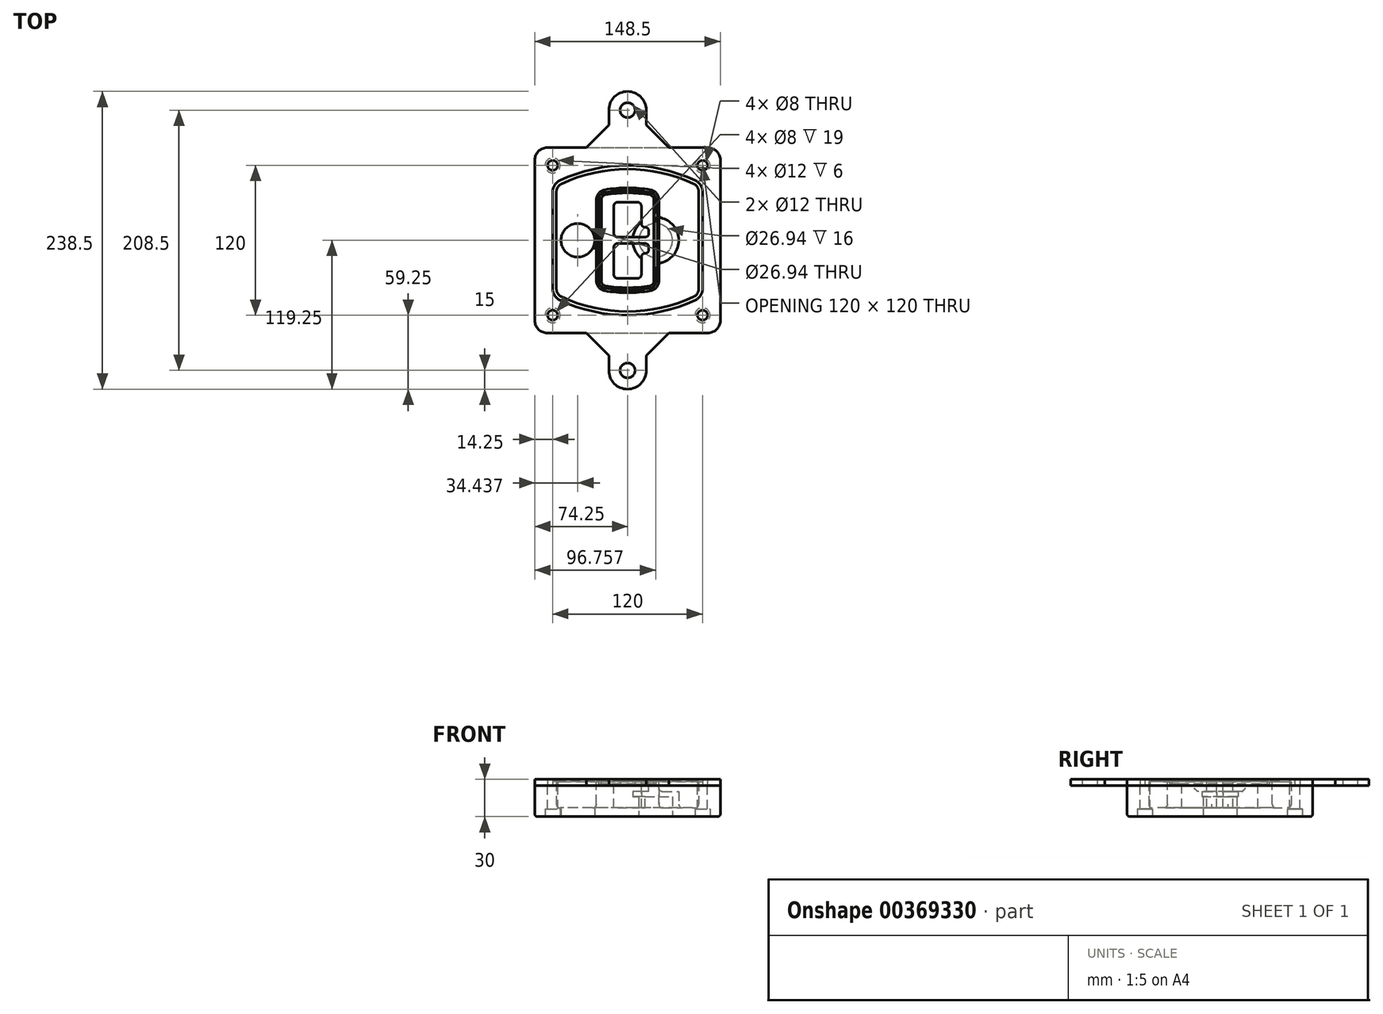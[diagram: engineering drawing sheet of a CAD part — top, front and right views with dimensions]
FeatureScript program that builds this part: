
annotation { "Feature Type Name" : "Feature", "Feature Type Description" : "" }
export const myFeature = defineFeature(function(context is Context, id is Id, definition is map)
    precondition{}
    {
        {
            var Q0;
            Q0=qCreatedBy(makeId("Top.planeOp"),FACE);
            var sketch = newSketch(context, id + "F0", { "sketchPlane" : qUnion([Q0])});
            skPoint(sketch, "E0.rect.middle", {"position": v(0, 0) * mm});
            skLineSegment(sketch, "E1.bottom", {"start": v(-64.25, -74.25) * mm, "end": v(64.25, -74.25) * mm});
            skLineSegment(sketch, "E1.top", {"start": v(-64.25, 74.25) * mm, "end": v(64.25, 74.25) * mm});
            skLineSegment(sketch, "E1.left", {"start": v(-74.25, -64.25) * mm, "end": v(-74.25, 64.25) * mm});
            skLineSegment(sketch, "E1.right", {"start": v(74.25, -64.25) * mm, "end": v(74.25, 64.25) * mm});
            skLineSegment(sketch, "E2", {"start": v(-74.25, 74.25) * mm, "end": v(74.25, -74.25) * mm, "construction": true});
            skLineSegment(sketch, "E3", {"start": v(74.25, 74.25) * mm, "end": v(-74.25, -74.25) * mm, "construction": true});
            skCircle(sketch, "E4", {"center": v(-60, 60) * mm, "radius": 4 * mm});
            skCircle(sketch, "E5", {"center": v(60, 60) * mm, "radius": 4 * mm});
            skCircle(sketch, "E6", {"center": v(60, -60) * mm, "radius": 4 * mm});
            skCircle(sketch, "E7", {"center": v(-60, -60) * mm, "radius": 4 * mm});
            skLineSegment(sketch, "E8", {"start": v(-60, 60) * mm, "end": v(60, 60) * mm, "construction": true});
            skLineSegment(sketch, "E9", {"start": v(60, 60) * mm, "end": v(60, -60) * mm, "construction": true});
            skLineSegment(sketch, "E10", {"start": v(60, -60) * mm, "end": v(-60, -60) * mm, "construction": true});
            skLineSegment(sketch, "E11", {"start": v(-60, -60) * mm, "end": v(-60, 60) * mm, "construction": true});
            skLineSegment(sketch, "E12", {"start": v(-60, 38.83) * mm, "end": v(-60, -38.83) * mm});
            skLineSegment(sketch, "E13", {"start": v(60, 38.83) * mm, "end": v(60, -38.83) * mm});
            skArc(sketch, "E14", {"start": v(54.26, 47.88) * mm, "mid": v(0, 60) * mm, "end": v(-54.26, 47.88) * mm});
            skArc(sketch, "E15", {"start": v(-54.26, -47.88) * mm, "mid": v(0, -60) * mm, "end": v(54.26, -47.88) * mm});
            skLineSegment(sketch, "E16", {"start": v(-60, 0) * mm, "end": v(60, 0) * mm, "construction": true});
            skPoint(sketch, "E17.visualSharp", {"position": v(-60, -45) * mm});
            skArc(sketch, "E17.filletArc", {"start": v(-60, -38.83) * mm, "mid": v(-58.44, -44.2) * mm, "end": v(-54.26, -47.88) * mm});
            skPoint(sketch, "E18.visualSharp", {"position": v(-60, 45) * mm});
            skArc(sketch, "E18.filletArc", {"start": v(-54.26, 47.88) * mm, "mid": v(-58.44, 44.2) * mm, "end": v(-60, 38.83) * mm});
            skPoint(sketch, "E19.visualSharp", {"position": v(60, 45) * mm});
            skArc(sketch, "E19.filletArc", {"start": v(60, 38.83) * mm, "mid": v(58.44, 44.2) * mm, "end": v(54.26, 47.88) * mm});
            skPoint(sketch, "E20.visualSharp", {"position": v(60, -45) * mm});
            skArc(sketch, "E20.filletArc", {"start": v(54.26, -47.88) * mm, "mid": v(58.44, -44.2) * mm, "end": v(60, -38.83) * mm});
            skPoint(sketch, "E21.visualSharp", {"position": v(-74.25, 74.25) * mm});
            skArc(sketch, "E21.filletArc", {"start": v(-64.25, 74.25) * mm, "mid": v(-71.32, 71.32) * mm, "end": v(-74.25, 64.25) * mm});
            skPoint(sketch, "E22.visualSharp", {"position": v(74.25, 74.25) * mm});
            skArc(sketch, "E22.filletArc", {"start": v(74.25, 64.25) * mm, "mid": v(71.32, 71.32) * mm, "end": v(64.25, 74.25) * mm});
            skPoint(sketch, "E23.visualSharp", {"position": v(74.25, -74.25) * mm});
            skArc(sketch, "E23.filletArc", {"start": v(64.25, -74.25) * mm, "mid": v(71.32, -71.32) * mm, "end": v(74.25, -64.25) * mm});
            skPoint(sketch, "E24.visualSharp", {"position": v(-74.25, -74.25) * mm});
            skArc(sketch, "E24.filletArc", {"start": v(-74.25, -64.25) * mm, "mid": v(-71.32, -71.32) * mm, "end": v(-64.25, -74.25) * mm});
            skArc(sketch, "E25.0", {"start": v(57, 38.83) * mm, "mid": v(55.9, 42.58) * mm, "end": v(52.98, 45.17) * mm});
            skLineSegment(sketch, "E25.1", {"start": v(57, 38.83) * mm, "end": v(57, -38.83) * mm});
            skArc(sketch, "E25.2", {"start": v(52.98, -45.17) * mm, "mid": v(55.9, -42.58) * mm, "end": v(57, -38.83) * mm});
            skArc(sketch, "E25.3", {"start": v(-52.98, -45.17) * mm, "mid": v(0, -57) * mm, "end": v(52.98, -45.17) * mm});
            skArc(sketch, "E25.4", {"start": v(-57, -38.83) * mm, "mid": v(-55.9, -42.58) * mm, "end": v(-52.98, -45.17) * mm});
            skArc(sketch, "E25.5", {"start": v(52.98, 45.17) * mm, "mid": v(0, 57) * mm, "end": v(-52.98, 45.17) * mm});
            skLineSegment(sketch, "E25.6", {"start": v(-57, 38.83) * mm, "end": v(-57, -38.83) * mm});
            skArc(sketch, "E25.7", {"start": v(-52.98, 45.17) * mm, "mid": v(-55.9, 42.58) * mm, "end": v(-57, 38.83) * mm});
            skArc(sketch, "E26.0", {"start": v(-55.96, 51.5) * mm, "mid": v(-61.82, 46.33) * mm, "end": v(-64, 38.83) * mm});
            skArc(sketch, "E26.1", {"start": v(55.96, 51.5) * mm, "mid": v(0, 64) * mm, "end": v(-55.96, 51.5) * mm});
            skArc(sketch, "E26.2", {"start": v(64, 38.83) * mm, "mid": v(61.82, 46.33) * mm, "end": v(55.96, 51.5) * mm});
            skLineSegment(sketch, "E26.3", {"start": v(64, 38.83) * mm, "end": v(64, -38.83) * mm});
            skArc(sketch, "E26.4", {"start": v(55.96, -51.5) * mm, "mid": v(61.82, -46.33) * mm, "end": v(64, -38.83) * mm});
            skLineSegment(sketch, "E26.5", {"start": v(-64, 38.83) * mm, "end": v(-64, -38.83) * mm});
            skArc(sketch, "E26.6", {"start": v(-55.96, -51.5) * mm, "mid": v(0, -64) * mm, "end": v(55.96, -51.5) * mm});
            skArc(sketch, "E26.7", {"start": v(-64, -38.83) * mm, "mid": v(-61.82, -46.33) * mm, "end": v(-55.96, -51.5) * mm});
            skSolve(sketch);
        }
        {
            var Q0;
            Q0=makeQuery(id+"F0.imprint","IMPRINT",FACE,{"disambiguationData":[TD([[makeQuery(id+"F0.imprint","IMPRINT",EDGE,{"derivedFrom":sQuery(id+"F0.wireOp",EDGE,"E1.bottom")}),1.0]])]});
            var Q1;
            Q1=makeQuery(id+"F0.imprint","IMPRINT",FACE,{"disambiguationData":[TD([[makeQuery(id+"F0.imprint","IMPRINT",EDGE,{"derivedFrom":sQuery(id+"F0.wireOp",EDGE,"E12")}),1.0]])]});
            var Q2;
            Q2=makeQuery(id+"F0.imprint","IMPRINT",FACE,{"disambiguationData":[TD([[makeQuery(id+"F0.imprint","IMPRINT",EDGE,{"derivedFrom":sQuery(id+"F0.wireOp",EDGE,"E25.0")}),1.0]])]});
            var Q3;
            Q3=makeQuery(id+"F0.imprint","IMPRINT",FACE,{"disambiguationData":[TD([[makeQuery(id+"F0.imprint","IMPRINT",EDGE,{"derivedFrom":sQuery(id+"F0.wireOp",EDGE,"E12")}),-1.0]])]});
            extrude(context, id + "F1", {"entities" : qUnion([Q0, Q1, Q2, Q3]), "oppositeDirection" : true, "depth" : 25 * mm});
        }
        {
            var Q0;
            Q0=makeQuery(id+"F0.imprint","IMPRINT",FACE,{"disambiguationData":[TD([[makeQuery(id+"F0.imprint","IMPRINT",EDGE,{"derivedFrom":sQuery(id+"F0.wireOp",EDGE,"E12")}),1.0]])]});
            extrude(context, id + "F2", {"entities" : qUnion([Q0]), "operationType" : NewBodyOperationType.ADD, "depth" : 3 * mm});
        }
        {
            var Q0;
            Q0=makeQuery(id+"F0.imprint","IMPRINT",FACE,{"disambiguationData":[TD([[makeQuery(id+"F0.imprint","IMPRINT",EDGE,{"derivedFrom":sQuery(id+"F0.wireOp",EDGE,"E25.0")}),1.0]])]});
            extrude(context, id + "F3", {"entities" : qUnion([Q0]), "operationType" : NewBodyOperationType.REMOVE, "oppositeDirection" : true, "depth" : 18 * mm});
        }
        {
            var Q0;
            Q0=makeQuery(id+"F2.opExtrude","CAP_FACE",FACE,{"disambiguationData":[OSD([sQuery(id+"F0.wireOp",EDGE,"E12"),sQuery(id+"F0.wireOp",EDGE,"E13"),sQuery(id+"F0.wireOp",EDGE,"E14"),sQuery(id+"F0.wireOp",EDGE,"E15"),sQuery(id+"F0.wireOp",EDGE,"E17.filletArc"),sQuery(id+"F0.wireOp",EDGE,"E18.filletArc"),sQuery(id+"F0.wireOp",EDGE,"E19.filletArc"),sQuery(id+"F0.wireOp",EDGE,"E20.filletArc"),sQuery(id+"F0.wireOp",EDGE,"E25.0"),sQuery(id+"F0.wireOp",EDGE,"E25.1"),sQuery(id+"F0.wireOp",EDGE,"E25.2"),sQuery(id+"F0.wireOp",EDGE,"E25.3"),sQuery(id+"F0.wireOp",EDGE,"E25.4"),sQuery(id+"F0.wireOp",EDGE,"E25.5"),sQuery(id+"F0.wireOp",EDGE,"E25.6"),sQuery(id+"F0.wireOp",EDGE,"E25.7")])],"isStart":false});
            var sketch = newSketch(context, id + "F4", { "sketchPlane" : qUnion([Q0])});
            skArc(sketch, "E27.0", {"start": v(-18.34, -40.45) * mm, "mid": v(0, -42) * mm, "end": v(18.34, -40.45) * mm});
            skArc(sketch, "E28.0", {"start": v(18.34, 40.45) * mm, "mid": v(0, 42) * mm, "end": v(-18.34, 40.45) * mm});
            skLineSegment(sketch, "E29", {"start": v(-25, 32.57) * mm, "end": v(-25, -32.57) * mm});
            skLineSegment(sketch, "E30", {"start": v(25, 32.57) * mm, "end": v(25, -32.57) * mm});
            skLineSegment(sketch, "E31", {"start": v(-25, 39.1) * mm, "end": v(25, 39.1) * mm, "construction": true});
            skLineSegment(sketch, "E32", {"start": v(-25, -39.1) * mm, "end": v(25, -39.1) * mm, "construction": true});
            skPoint(sketch, "E33.visualSharp", {"position": v(-25, 39.1) * mm});
            skArc(sketch, "E33.filletArc", {"start": v(-18.34, 40.45) * mm, "mid": v(-23.11, 37.73) * mm, "end": v(-25, 32.57) * mm});
            skPoint(sketch, "E34.visualSharp", {"position": v(25, 39.1) * mm});
            skArc(sketch, "E34.filletArc", {"start": v(25, 32.57) * mm, "mid": v(23.11, 37.73) * mm, "end": v(18.34, 40.45) * mm});
            skPoint(sketch, "E35.visualSharp", {"position": v(25, -39.1) * mm});
            skArc(sketch, "E35.filletArc", {"start": v(18.34, -40.45) * mm, "mid": v(23.11, -37.73) * mm, "end": v(25, -32.57) * mm});
            skPoint(sketch, "E36.visualSharp", {"position": v(-25, -39.1) * mm});
            skArc(sketch, "E36.filletArc", {"start": v(-25, -32.57) * mm, "mid": v(-23.11, -37.73) * mm, "end": v(-18.34, -40.45) * mm});
            skArc(sketch, "E37.0", {"start": v(52.98, 45.17) * mm, "mid": v(0, 57) * mm, "end": v(-52.98, 45.17) * mm});
            skArc(sketch, "E37.1", {"start": v(-52.98, 45.17) * mm, "mid": v(-55.9, 42.58) * mm, "end": v(-57, 38.83) * mm});
            skLineSegment(sketch, "E37.2", {"start": v(-57, 38.83) * mm, "end": v(-57, -38.83) * mm});
            skArc(sketch, "E37.3", {"start": v(-57, -38.83) * mm, "mid": v(-55.9, -42.58) * mm, "end": v(-52.98, -45.17) * mm});
            skArc(sketch, "E37.4", {"start": v(-52.98, -45.17) * mm, "mid": v(0, -57) * mm, "end": v(52.98, -45.17) * mm});
            skArc(sketch, "E37.5", {"start": v(52.98, -45.17) * mm, "mid": v(55.9, -42.58) * mm, "end": v(57, -38.83) * mm});
            skLineSegment(sketch, "E37.6", {"start": v(57, 38.83) * mm, "end": v(57, -38.83) * mm});
            skArc(sketch, "E37.7", {"start": v(57, 38.83) * mm, "mid": v(55.9, 42.58) * mm, "end": v(52.98, 45.17) * mm});
            skLineSegment(sketch, "E38.0", {"start": v(23, 32.57) * mm, "end": v(23, -32.57) * mm});
            skArc(sketch, "E38.1", {"start": v(18, -38.48) * mm, "mid": v(21.58, -36.44) * mm, "end": v(23, -32.57) * mm});
            skArc(sketch, "E38.2", {"start": v(-18, -38.48) * mm, "mid": v(0, -40) * mm, "end": v(18, -38.48) * mm});
            skArc(sketch, "E38.3", {"start": v(-23, -32.57) * mm, "mid": v(-21.58, -36.44) * mm, "end": v(-18, -38.48) * mm});
            skLineSegment(sketch, "E38.4", {"start": v(-23, 32.57) * mm, "end": v(-23, -32.57) * mm});
            skArc(sketch, "E38.5", {"start": v(23, 32.57) * mm, "mid": v(21.58, 36.44) * mm, "end": v(18, 38.48) * mm});
            skArc(sketch, "E38.6", {"start": v(-18, 38.48) * mm, "mid": v(-21.58, 36.44) * mm, "end": v(-23, 32.57) * mm});
            skArc(sketch, "E38.7", {"start": v(18, 38.48) * mm, "mid": v(0, 40) * mm, "end": v(-18, 38.48) * mm});
            skArc(sketch, "E39.0", {"start": v(21, 32.57) * mm, "mid": v(20.06, 35.15) * mm, "end": v(17.67, 36.5) * mm});
            skLineSegment(sketch, "E39.1", {"start": v(21, 32.57) * mm, "end": v(21, -32.57) * mm});
            skArc(sketch, "E39.2", {"start": v(17.67, -36.5) * mm, "mid": v(20.06, -35.15) * mm, "end": v(21, -32.57) * mm});
            skArc(sketch, "E39.3", {"start": v(-17.67, -36.5) * mm, "mid": v(0, -38) * mm, "end": v(17.67, -36.5) * mm});
            skArc(sketch, "E39.4", {"start": v(-21, -32.57) * mm, "mid": v(-20.06, -35.15) * mm, "end": v(-17.67, -36.5) * mm});
            skArc(sketch, "E39.5", {"start": v(17.67, 36.5) * mm, "mid": v(0, 38) * mm, "end": v(-17.67, 36.5) * mm});
            skLineSegment(sketch, "E39.6", {"start": v(-21, 32.57) * mm, "end": v(-21, -32.57) * mm});
            skArc(sketch, "E39.7", {"start": v(-17.67, 36.5) * mm, "mid": v(-20.06, 35.15) * mm, "end": v(-21, 32.57) * mm});
            skLineSegment(sketch, "E40", {"start": v(-25, 0) * mm, "end": v(25, 0) * mm, "construction": true});
            skLineSegment(sketch, "E41", {"start": v(-11, 5.5) * mm, "end": v(-11, 27.5) * mm});
            skLineSegment(sketch, "E42", {"start": v(-8, 30.5) * mm, "end": v(8, 30.5) * mm});
            skLineSegment(sketch, "E43", {"start": v(11, 27.5) * mm, "end": v(11, 13.5) * mm});
            skLineSegment(sketch, "E44", {"start": v(14, 10.5) * mm, "end": v(14, 10.5) * mm});
            skLineSegment(sketch, "E45", {"start": v(17, 7.5) * mm, "end": v(17, 5.5) * mm});
            skLineSegment(sketch, "E46", {"start": v(14, 2.5) * mm, "end": v(-8, 2.5) * mm});
            skPoint(sketch, "E47.visualSharp", {"position": v(-11, 30.5) * mm});
            skArc(sketch, "E47.filletArc", {"start": v(-8, 30.5) * mm, "mid": v(-10.12, 29.62) * mm, "end": v(-11, 27.5) * mm});
            skPoint(sketch, "E48.visualSharp", {"position": v(11, 30.5) * mm});
            skArc(sketch, "E48.filletArc", {"start": v(11, 27.5) * mm, "mid": v(10.12, 29.62) * mm, "end": v(8, 30.5) * mm});
            skPoint(sketch, "E49.visualSharp", {"position": v(11, 10.5) * mm});
            skArc(sketch, "E49.filletArc", {"start": v(11, 13.5) * mm, "mid": v(11.88, 11.38) * mm, "end": v(14, 10.5) * mm});
            skPoint(sketch, "E50.visualSharp", {"position": v(17, 10.5) * mm});
            skArc(sketch, "E50.filletArc", {"start": v(17, 7.5) * mm, "mid": v(16.12, 9.62) * mm, "end": v(14, 10.5) * mm});
            skPoint(sketch, "E51.visualSharp", {"position": v(17, 2.5) * mm});
            skArc(sketch, "E51.filletArc", {"start": v(14, 2.5) * mm, "mid": v(16.12, 3.38) * mm, "end": v(17, 5.5) * mm});
            skPoint(sketch, "E52.visualSharp", {"position": v(-11, 2.5) * mm});
            skArc(sketch, "E52.filletArc", {"start": v(-11, 5.5) * mm, "mid": v(-10.12, 3.38) * mm, "end": v(-8, 2.5) * mm});
            skLineSegment(sketch, "E53.0.MirrorCS", {"start": v(14, -2.5) * mm, "end": v(-8, -2.5) * mm});
            skArc(sketch, "E54.0.MirrorCS", {"start": v(-11, -5.5) * mm, "mid": v(-10.12, -3.38) * mm, "end": v(-8, -2.5) * mm});
            skLineSegment(sketch, "E55.0.MirrorCS", {"start": v(-11, -5.5) * mm, "end": v(-11, -27.5) * mm});
            skArc(sketch, "E56.0.MirrorCS", {"start": v(-8, -30.5) * mm, "mid": v(-10.12, -29.62) * mm, "end": v(-11, -27.5) * mm});
            skLineSegment(sketch, "E57.0.MirrorCS", {"start": v(-8, -30.5) * mm, "end": v(8, -30.5) * mm});
            skArc(sketch, "E58.0.MirrorCS", {"start": v(11, -27.5) * mm, "mid": v(10.12, -29.62) * mm, "end": v(8, -30.5) * mm});
            skLineSegment(sketch, "E59.0.MirrorCS", {"start": v(11, -27.5) * mm, "end": v(11, -13.5) * mm});
            skArc(sketch, "E60.0.MirrorCS", {"start": v(11, -13.5) * mm, "mid": v(11.88, -11.38) * mm, "end": v(14, -10.5) * mm});
            skArc(sketch, "E61.0.MirrorCS", {"start": v(17, -7.5) * mm, "mid": v(16.12, -9.62) * mm, "end": v(14, -10.5) * mm});
            skLineSegment(sketch, "E62.0.MirrorCS", {"start": v(17, -7.5) * mm, "end": v(17, -5.5) * mm});
            skArc(sketch, "E63.0.MirrorCS", {"start": v(14, -2.5) * mm, "mid": v(16.12, -3.38) * mm, "end": v(17, -5.5) * mm});
            skSolve(sketch);
        }
        {
            var Q0;
            Q0=makeQuery(id+"F4.imprint","IMPRINT",FACE,{"disambiguationData":[TD([[makeQuery(id+"F4.imprint","IMPRINT",EDGE,{"derivedFrom":sQuery(id+"F4.wireOp",EDGE,"E27.0")}),1.0]])]});
            var Q1;
            Q1=makeQuery(id+"F4.imprint","IMPRINT",FACE,{"disambiguationData":[TD([[makeQuery(id+"F4.imprint","IMPRINT",EDGE,{"derivedFrom":sQuery(id+"F4.wireOp",EDGE,"E38.0")}),-1.0]])]});
            var Q2;
            Q2=makeQuery(id+"F4.imprint","IMPRINT",FACE,{"disambiguationData":[TD([[makeQuery(id+"F4.imprint","IMPRINT",EDGE,{"derivedFrom":sQuery(id+"F4.wireOp",EDGE,"E39.0")}),1.0]])]});
            extrude(context, id + "F5", {"entities" : qUnion([Q0, Q1, Q2]), "operationType" : NewBodyOperationType.ADD, "endBound" : BoundingType.UP_TO_NEXT, "oppositeDirection" : true, "depth" : 25 * mm});
        }
        {
            var Q0;
            Q0=makeQuery(id+"F4.imprint","IMPRINT",FACE,{"disambiguationData":[TD([[makeQuery(id+"F4.imprint","IMPRINT",EDGE,{"derivedFrom":sQuery(id+"F4.wireOp",EDGE,"E38.0")}),-1.0]])]});
            extrude(context, id + "F6", {"entities" : qUnion([Q0]), "operationType" : NewBodyOperationType.REMOVE, "oppositeDirection" : true, "depth" : 2 * mm});
        }
        {
            var Q0;
            Q0=makeQuery(id+"F1.opExtrude","CAP_FACE",FACE,{"disambiguationData":[OSD([sQuery(id+"F0.wireOp",EDGE,"E1.bottom"),sQuery(id+"F0.wireOp",EDGE,"E1.top"),sQuery(id+"F0.wireOp",EDGE,"E1.left"),sQuery(id+"F0.wireOp",EDGE,"E1.right"),sQuery(id+"F0.wireOp",EDGE,"E4"),sQuery(id+"F0.wireOp",EDGE,"E5"),sQuery(id+"F0.wireOp",EDGE,"E6"),sQuery(id+"F0.wireOp",EDGE,"E7"),sQuery(id+"F0.wireOp",EDGE,"E21.filletArc"),sQuery(id+"F0.wireOp",EDGE,"E22.filletArc"),sQuery(id+"F0.wireOp",EDGE,"E23.filletArc"),sQuery(id+"F0.wireOp",EDGE,"E24.filletArc")])],"isStart":false});
            var sketch = newSketch(context, id + "F7", { "sketchPlane" : qUnion([Q0])});
            skCircle(sketch, "E64", {"center": v(22.5, 0) * mm, "radius": 13.47 * mm});
            skCircle(sketch, "E65", {"center": v(-39.81, 0) * mm, "radius": 13.47 * mm});
            skLineSegment(sketch, "E66", {"start": v(74.25, 0) * mm, "end": v(-74.25, 0) * mm});
            skCircle(sketch, "E67", {"center": v(22.5, 0) * mm, "radius": 18.47 * mm});
            skCircle(sketch, "E68", {"center": v(60, -60) * mm, "radius": 6 * mm});
            skCircle(sketch, "E69", {"center": v(-60, -60) * mm, "radius": 6 * mm});
            skCircle(sketch, "E70", {"center": v(-60, 60) * mm, "radius": 6 * mm});
            skCircle(sketch, "E71", {"center": v(60, 60) * mm, "radius": 6 * mm});
            skSolve(sketch);
        }
        {
            var Q0;
            {var subQ1=sQuery(id+"F7.wireOp",EDGE,"E66");var subQ4=sQuery(id+"F7.wireOp",EDGE,"E64");var subQ6=makeQuery(id+"F7.imprint","INTERSECT",VERTEX,{"disambiguationData":[OD(0.0)],"derivedFrom":[subQ4,subQ1]});Q0=makeQuery(id+"F7.imprint","IMPRINT",FACE,{"disambiguationData":[TD([[makeQuery(id+"F7.imprint","IMPRINT",EDGE,{"disambiguationData":[TD([[subQ6,-1.0]])],"derivedFrom":subQ4}),-1.0]])]});}
            var Q1;
            {var subQ0=sQuery(id+"F7.wireOp",EDGE,"E66");var subQ1=sQuery(id+"F7.wireOp",EDGE,"E64");var subQ3=makeQuery(id+"F7.imprint","INTERSECT",VERTEX,{"disambiguationData":[OD(0.0)],"derivedFrom":[subQ1,subQ0]});Q1=makeQuery(id+"F7.imprint","IMPRINT",FACE,{"disambiguationData":[TD([[makeQuery(id+"F7.imprint","IMPRINT",EDGE,{"disambiguationData":[TD([[subQ3,-1.0]])],"derivedFrom":subQ1}),1.0]])]});}
            var Q2;
            {var subQ0=sQuery(id+"F7.wireOp",EDGE,"E66");var subQ1=sQuery(id+"F7.wireOp",EDGE,"E64");var subQ3=makeQuery(id+"F7.imprint","INTERSECT",VERTEX,{"disambiguationData":[OD(0.0)],"derivedFrom":[subQ1,subQ0]});Q2=makeQuery(id+"F7.imprint","IMPRINT",FACE,{"disambiguationData":[TD([[makeQuery(id+"F7.imprint","IMPRINT",EDGE,{"disambiguationData":[TD([[subQ3,1.0]])],"derivedFrom":subQ1}),1.0]])]});}
            var Q3;
            {var subQ1=sQuery(id+"F7.wireOp",EDGE,"E66");var subQ4=sQuery(id+"F7.wireOp",EDGE,"E64");var subQ6=makeQuery(id+"F7.imprint","INTERSECT",VERTEX,{"disambiguationData":[OD(0.0)],"derivedFrom":[subQ4,subQ1]});Q3=makeQuery(id+"F7.imprint","IMPRINT",FACE,{"disambiguationData":[TD([[makeQuery(id+"F7.imprint","IMPRINT",EDGE,{"disambiguationData":[TD([[subQ6,1.0]])],"derivedFrom":subQ4}),-1.0]])]});}
            extrude(context, id + "F8", {"entities" : qUnion([Q0, Q1, Q2, Q3]), "operationType" : NewBodyOperationType.ADD, "oppositeDirection" : true, "depth" : 20 * mm});
        }
        {
            var Q0;
            {var subQ0=sQuery(id+"F7.wireOp",EDGE,"E66");var subQ1=sQuery(id+"F7.wireOp",EDGE,"E64");var subQ3=makeQuery(id+"F7.imprint","INTERSECT",VERTEX,{"disambiguationData":[OD(0.0)],"derivedFrom":[subQ1,subQ0]});Q0=makeQuery(id+"F7.imprint","IMPRINT",FACE,{"disambiguationData":[TD([[makeQuery(id+"F7.imprint","IMPRINT",EDGE,{"disambiguationData":[TD([[subQ3,-1.0]])],"derivedFrom":subQ1}),1.0]])]});}
            var Q1;
            {var subQ0=sQuery(id+"F7.wireOp",EDGE,"E66");var subQ1=sQuery(id+"F7.wireOp",EDGE,"E64");var subQ3=makeQuery(id+"F7.imprint","INTERSECT",VERTEX,{"disambiguationData":[OD(0.0)],"derivedFrom":[subQ1,subQ0]});Q1=makeQuery(id+"F7.imprint","IMPRINT",FACE,{"disambiguationData":[TD([[makeQuery(id+"F7.imprint","IMPRINT",EDGE,{"disambiguationData":[TD([[subQ3,1.0]])],"derivedFrom":subQ1}),1.0]])]});}
            extrude(context, id + "F9", {"entities" : qUnion([Q0, Q1]), "operationType" : NewBodyOperationType.REMOVE, "oppositeDirection" : true, "depth" : 16 * mm});
        }
        {
            var Q0;
            {var subQ0=sQuery(id+"F7.wireOp",EDGE,"E66");var subQ1=sQuery(id+"F7.wireOp",EDGE,"E65");var subQ3=makeQuery(id+"F7.imprint","INTERSECT",VERTEX,{"disambiguationData":[OD(0.0)],"derivedFrom":[subQ1,subQ0]});Q0=makeQuery(id+"F7.imprint","IMPRINT",FACE,{"disambiguationData":[TD([[makeQuery(id+"F7.imprint","IMPRINT",EDGE,{"disambiguationData":[TD([[subQ3,-1.0]])],"derivedFrom":subQ1}),1.0]])]});}
            var Q1;
            {var subQ0=sQuery(id+"F7.wireOp",EDGE,"E66");var subQ1=sQuery(id+"F7.wireOp",EDGE,"E65");var subQ3=makeQuery(id+"F7.imprint","INTERSECT",VERTEX,{"disambiguationData":[OD(0.0)],"derivedFrom":[subQ1,subQ0]});Q1=makeQuery(id+"F7.imprint","IMPRINT",FACE,{"disambiguationData":[TD([[makeQuery(id+"F7.imprint","IMPRINT",EDGE,{"disambiguationData":[TD([[subQ3,1.0]])],"derivedFrom":subQ1}),1.0]])]});}
            extrude(context, id + "F10", {"entities" : qUnion([Q0, Q1]), "operationType" : NewBodyOperationType.REMOVE, "oppositeDirection" : true, "depth" : 25 * mm});
        }
        {
            var Q0;
            Q0=makeQuery(id+"F7.imprint","IMPRINT",FACE,{"disambiguationData":[TD([[makeQuery(id+"F7.imprint","IMPRINT",EDGE,{"derivedFrom":sQuery(id+"F7.wireOp",EDGE,"E68")}),1.0]])]});
            var Q1;
            Q1=makeQuery(id+"F7.imprint","IMPRINT",FACE,{"disambiguationData":[TD([[makeQuery(id+"F7.imprint","IMPRINT",EDGE,{"derivedFrom":makeQuery(id+"F1.opExtrude","CAP_EDGE",EDGE,{"disambiguationData":[OSD([sQuery(id+"F0.wireOp",EDGE,"E5")])],"isStart":false})}),-1.0]])]});
            var Q2;
            Q2=makeQuery(id+"F7.imprint","IMPRINT",FACE,{"disambiguationData":[TD([[makeQuery(id+"F7.imprint","IMPRINT",EDGE,{"derivedFrom":sQuery(id+"F7.wireOp",EDGE,"E69")}),1.0]])]});
            var Q3;
            Q3=makeQuery(id+"F7.imprint","IMPRINT",FACE,{"disambiguationData":[TD([[makeQuery(id+"F7.imprint","IMPRINT",EDGE,{"derivedFrom":makeQuery(id+"F1.opExtrude","CAP_EDGE",EDGE,{"disambiguationData":[OSD([sQuery(id+"F0.wireOp",EDGE,"E4")])],"isStart":false})}),-1.0]])]});
            var Q4;
            Q4=makeQuery(id+"F7.imprint","IMPRINT",FACE,{"disambiguationData":[TD([[makeQuery(id+"F7.imprint","IMPRINT",EDGE,{"derivedFrom":sQuery(id+"F7.wireOp",EDGE,"E70")}),1.0]])]});
            var Q5;
            Q5=makeQuery(id+"F7.imprint","IMPRINT",FACE,{"disambiguationData":[TD([[makeQuery(id+"F7.imprint","IMPRINT",EDGE,{"derivedFrom":makeQuery(id+"F1.opExtrude","CAP_EDGE",EDGE,{"disambiguationData":[OSD([sQuery(id+"F0.wireOp",EDGE,"E7")])],"isStart":false})}),-1.0]])]});
            var Q6;
            Q6=makeQuery(id+"F7.imprint","IMPRINT",FACE,{"disambiguationData":[TD([[makeQuery(id+"F7.imprint","IMPRINT",EDGE,{"derivedFrom":sQuery(id+"F7.wireOp",EDGE,"E71")}),1.0]])]});
            var Q7;
            Q7=makeQuery(id+"F7.imprint","IMPRINT",FACE,{"disambiguationData":[TD([[makeQuery(id+"F7.imprint","IMPRINT",EDGE,{"derivedFrom":makeQuery(id+"F1.opExtrude","CAP_EDGE",EDGE,{"disambiguationData":[OSD([sQuery(id+"F0.wireOp",EDGE,"E6")])],"isStart":false})}),-1.0]])]});
            extrude(context, id + "F11", {"entities" : qUnion([Q0, Q1, Q2, Q3, Q4, Q5, Q6, Q7]), "operationType" : NewBodyOperationType.REMOVE, "oppositeDirection" : true, "depth" : 6 * mm});
        }
        {
            var Q0;
            Q0=makeQuery(id+"F9.boolean.opBoolean","COPY",FACE,{"derivedFrom":makeQuery(id+"F9.opExtrude","CAP_FACE",FACE,{"disambiguationData":[OSD([sQuery(id+"F7.wireOp",EDGE,"E64")])],"isStart":false})});
            var sketch = newSketch(context, id + "F12", { "sketchPlane" : qUnion([Q0])});
            skArc(sketch, "E72.0", {"start": v(11, 14.45) * mm, "mid": v(6.45, 9.13) * mm, "end": v(4.2, 2.5) * mm});
            skArc(sketch, "E72.1", {"start": v(4.2, -2.5) * mm, "mid": v(6.45, -9.13) * mm, "end": v(11, -14.45) * mm});
            skLineSegment(sketch, "E73", {"start": v(4.2, -2.5) * mm, "end": v(14, -2.5) * mm});
            skLineSegment(sketch, "E74.0", {"start": v(14, 2.5) * mm, "end": v(4.2, 2.5) * mm});
            skArc(sketch, "E74.1", {"start": v(14, 2.5) * mm, "mid": v(16.12, 3.38) * mm, "end": v(17, 5.5) * mm});
            skLineSegment(sketch, "E74.2", {"start": v(17, 7.5) * mm, "end": v(17, 5.5) * mm});
            skArc(sketch, "E74.3", {"start": v(17, 7.5) * mm, "mid": v(16.12, 9.62) * mm, "end": v(14, 10.5) * mm});
            skArc(sketch, "E74.4", {"start": v(11, 13.5) * mm, "mid": v(11.88, 11.38) * mm, "end": v(14, 10.5) * mm});
            skLineSegment(sketch, "E74.5", {"start": v(11, 14.45) * mm, "end": v(11, 13.5) * mm});
            skLineSegment(sketch, "E74.7", {"start": v(14, -2.5) * mm, "end": v(4.2, -2.5) * mm});
            skArc(sketch, "E74.8", {"start": v(14, -2.5) * mm, "mid": v(16.12, -3.38) * mm, "end": v(17, -5.5) * mm});
            skLineSegment(sketch, "E74.9", {"start": v(17, -7.5) * mm, "end": v(17, -5.5) * mm});
            skArc(sketch, "E74.10", {"start": v(17, -7.5) * mm, "mid": v(16.12, -9.62) * mm, "end": v(14, -10.5) * mm});
            skArc(sketch, "E74.11", {"start": v(11, -13.5) * mm, "mid": v(11.88, -11.38) * mm, "end": v(14, -10.5) * mm});
            skLineSegment(sketch, "E74.12", {"start": v(11, -14.45) * mm, "end": v(11, -13.5) * mm});
            skPoint(sketch, "E75.orphan", {"position": v(11, -27.5) * mm});
            skPoint(sketch, "E76.orphan", {"position": v(-8, -2.5) * mm});
            skPoint(sketch, "E77.orphan", {"position": v(-8, 2.5) * mm});
            skPoint(sketch, "E78.orphan", {"position": v(11, 27.5) * mm});
            skSolve(sketch);
        }
        {
            var Q0;
            {var subQ7=sQuery(id+"F12.wireOp",EDGE,"E72.0");var subQ14=sQuery(id+"F12.wireOp",EDGE,"E72.1");var subQ16=sQuery(id+"F12.wireOp",EDGE,"E74.1");var subQ18=sQuery(id+"F12.wireOp",EDGE,"E74.8");Q0=qUnion([makeQuery(id+"F12.imprint","IMPRINT",FACE,{"disambiguationData":[TD([[makeQuery(id+"F12.imprint","IMPRINT",EDGE,{"derivedFrom":subQ7}),1.0]])]}),makeQuery(id+"F12.imprint","IMPRINT",FACE,{"disambiguationData":[TD([[makeQuery(id+"F12.imprint","IMPRINT",EDGE,{"derivedFrom":subQ14}),1.0]])]}),makeQuery(id+"F12.imprint","IMPRINT",FACE,{"disambiguationData":[TD([[makeQuery(id+"F12.imprint","IMPRINT",EDGE,{"derivedFrom":subQ16}),1.0]])]}),makeQuery(id+"F12.imprint","IMPRINT",FACE,{"disambiguationData":[TD([[makeQuery(id+"F12.imprint","IMPRINT",EDGE,{"derivedFrom":subQ18}),-1.0]])]})]);}
            var Q1;
            Q1=makeQuery(id+"F5.boolean.opBoolean","SPLIT",FACE,{"disambiguationData":[TD([makeQuery(id+"F5.opExtrude","SWEPT_FACE",FACE,{"disambiguationData":[OSD([sQuery(id+"F4.wireOp",EDGE,"E41")])]})])],"derivedFrom":makeQuery(id+"F3.boolean.opBoolean","COPY",FACE,{"derivedFrom":makeQuery(id+"F3.opExtrude","CAP_FACE",FACE,{"disambiguationData":[OSD([sQuery(id+"F0.wireOp",EDGE,"E25.0"),sQuery(id+"F0.wireOp",EDGE,"E25.1"),sQuery(id+"F0.wireOp",EDGE,"E25.2"),sQuery(id+"F0.wireOp",EDGE,"E25.3"),sQuery(id+"F0.wireOp",EDGE,"E25.4"),sQuery(id+"F0.wireOp",EDGE,"E25.5"),sQuery(id+"F0.wireOp",EDGE,"E25.6"),sQuery(id+"F0.wireOp",EDGE,"E25.7")])],"isStart":false})})});
            extrude(context, id + "F13", {"entities" : qUnion([Q0]), "operationType" : NewBodyOperationType.REMOVE, "endBound" : BoundingType.UP_TO_SURFACE, "endBoundEntityFace" : qUnion([Q1]), "depth" : 25 * mm});
        }
        {
            var Q0;
            Q0=makeQuery(id+"F3.boolean.opBoolean","COPY",EDGE,{"derivedFrom":makeQuery(id+"F3.opExtrude","CAP_EDGE",EDGE,{"disambiguationData":[OSD([sQuery(id+"F0.wireOp",EDGE,"E25.6")])],"isStart":false})});
            var Q1;
            Q1=makeQuery(id+"F8.boolean.opBoolean","INTERSECT",EDGE,{"derivedFrom":[makeQuery(id+"F5.opExtrude","SWEPT_FACE",FACE,{"disambiguationData":[OSD([sQuery(id+"F4.wireOp",EDGE,"E30")])]}),makeQuery(id+"F8.opExtrude","CAP_FACE",FACE,{"disambiguationData":[OSD([sQuery(id+"F7.wireOp",EDGE,"E67")])],"isStart":false})]});
            var Q2;
            Q2=makeQuery(id+"F8.boolean.opBoolean","INTERSECT",EDGE,{"disambiguationData":[OD(1.0)],"derivedFrom":[makeQuery(id+"F5.opExtrude","SWEPT_FACE",FACE,{"disambiguationData":[OSD([sQuery(id+"F4.wireOp",EDGE,"E30")])]}),makeQuery(id+"F8.opExtrude","SWEPT_FACE",FACE,{"disambiguationData":[OSD([sQuery(id+"F7.wireOp",EDGE,"E67")])]})]});
            var Q3;
            {var subQ0=sQuery(id+"F4.wireOp",EDGE,"E30");Q3=makeQuery(id+"F8.boolean.opBoolean","SPLIT",EDGE,{"disambiguationData":[TD([makeQuery(id+"F5.opExtrude","SWEPT_FACE",FACE,{"disambiguationData":[OSD([sQuery(id+"F4.wireOp",EDGE,"E35.filletArc")])]})])],"derivedFrom":makeQuery(id+"F5.opExtrude","CAP_EDGE",EDGE,{"disambiguationData":[OSD([subQ0])],"isStart":false})});}
            var Q4;
            {var subQ0=sQuery(id+"F0.wireOp",EDGE,"E25.7");var subQ1=sQuery(id+"F0.wireOp",EDGE,"E25.1");var subQ2=sQuery(id+"F0.wireOp",EDGE,"E25.6");var subQ3=sQuery(id+"F0.wireOp",EDGE,"E25.5");var subQ4=sQuery(id+"F0.wireOp",EDGE,"E25.4");var subQ5=sQuery(id+"F0.wireOp",EDGE,"E25.0");var subQ6=sQuery(id+"F0.wireOp",EDGE,"E25.2");var subQ7=sQuery(id+"F0.wireOp",EDGE,"E25.3");Q4=makeQuery(id+"F8.boolean.opBoolean","INTERSECT",EDGE,{"derivedFrom":[makeQuery(id+"F5.boolean.opBoolean","SPLIT",FACE,{"disambiguationData":[TD([makeQuery(id+"F2.opExtrude","SWEPT_FACE",FACE,{"disambiguationData":[OSD([subQ5])]})])],"derivedFrom":makeQuery(id+"F3.boolean.opBoolean","COPY",FACE,{"derivedFrom":makeQuery(id+"F3.opExtrude","CAP_FACE",FACE,{"disambiguationData":[OSD([subQ5,subQ1,subQ6,subQ7,subQ4,subQ3,subQ2,subQ0])],"isStart":false})})}),makeQuery(id+"F8.opExtrude","SWEPT_FACE",FACE,{"disambiguationData":[OSD([sQuery(id+"F7.wireOp",EDGE,"E67")])]})]});}
            var Q5;
            Q5=makeQuery(id+"F8.boolean.opBoolean","INTERSECT",EDGE,{"disambiguationData":[OD(0.0)],"derivedFrom":[makeQuery(id+"F5.opExtrude","SWEPT_FACE",FACE,{"disambiguationData":[OSD([sQuery(id+"F4.wireOp",EDGE,"E30")])]}),makeQuery(id+"F8.opExtrude","SWEPT_FACE",FACE,{"disambiguationData":[OSD([sQuery(id+"F7.wireOp",EDGE,"E67")])]})]});
            fillet(context, id + "F14", {"entities" : qUnion([Q0, Q1, Q2, Q3, Q4, Q5]), "radius" : 3 * mm, "tangentPropagation" : true, "allowEdgeOverflow" : false});
        }
        {
            var Q0;
            Q0=makeQuery(id+"F1.opExtrude","CAP_EDGE",EDGE,{"disambiguationData":[OSD([sQuery(id+"F0.wireOp",EDGE,"E1.bottom")])],"isStart":false});
            fillet(context, id + "F15", {"entities" : qUnion([Q0]), "radius" : 2 * mm, "tangentPropagation" : true, "allowEdgeOverflow" : false});
        }
        {
            var Q0;
            {var subQ0=sQuery(id+"F0.wireOp",EDGE,"E21.filletArc");var subQ1=sQuery(id+"F0.wireOp",EDGE,"E7");var subQ2=sQuery(id+"F0.wireOp",EDGE,"E6");var subQ3=sQuery(id+"F0.wireOp",EDGE,"E5");var subQ4=sQuery(id+"F0.wireOp",EDGE,"E4");var subQ5=sQuery(id+"F0.wireOp",EDGE,"E22.filletArc");var subQ6=sQuery(id+"F0.wireOp",EDGE,"E1.bottom");var subQ7=sQuery(id+"F0.wireOp",EDGE,"E1.right");var subQ8=sQuery(id+"F0.wireOp",EDGE,"E1.top");var subQ9=sQuery(id+"F0.wireOp",EDGE,"E1.left");var subQ10=sQuery(id+"F0.wireOp",EDGE,"E23.filletArc");var subQ11=sQuery(id+"F0.wireOp",EDGE,"E24.filletArc");Q0=makeQuery(id+"F2.boolean.opBoolean","SPLIT",FACE,{"disambiguationData":[TD([makeQuery(id+"F1.opExtrude","SWEPT_FACE",FACE,{"disambiguationData":[OSD([subQ6])]})])],"derivedFrom":makeQuery(id+"F1.opExtrude","CAP_FACE",FACE,{"disambiguationData":[OSD([subQ6,subQ8,subQ9,subQ7,subQ4,subQ3,subQ2,subQ1,subQ0,subQ5,subQ10,subQ11])],"isStart":true})});}
            var sketch = newSketch(context, id + "F16", { "sketchPlane" : qUnion([Q0])});
            skLineSegment(sketch, "E79", {"start": v(0, 74.25) * mm, "end": v(0, 104.25) * mm, "construction": true});
            skCircle(sketch, "E80", {"center": v(0, 104.25) * mm, "radius": 6 * mm});
            skArc(sketch, "E81", {"start": v(15, 104.25) * mm, "mid": v(0, 119.25) * mm, "end": v(-15, 104.25) * mm});
            skLineSegment(sketch, "E82", {"start": v(-15, 104.25) * mm, "end": v(-15, 92.25) * mm});
            skLineSegment(sketch, "E83", {"start": v(-15, 92.25) * mm, "end": v(-33, 74.25) * mm});
            skLineSegment(sketch, "E84", {"start": v(15, 104.25) * mm, "end": v(15, 92.25) * mm});
            skLineSegment(sketch, "E85", {"start": v(15, 92.25) * mm, "end": v(33, 74.25) * mm});
            skArc(sketch, "E86.MirrorCS", {"start": v(-15, 104.25) * mm, "mid": v(0, 119.25) * mm, "end": v(15, 104.25) * mm});
            skLineSegment(sketch, "E87.MirrorCS", {"start": v(-135.56, 0) * mm, "end": v(134.84, 0) * mm});
            skLineSegment(sketch, "E88.MirrorCS", {"start": v(-15, -104.25) * mm, "end": v(-15, -92.25) * mm});
            skLineSegment(sketch, "E89.MirrorCS", {"start": v(15, -104.25) * mm, "end": v(15, -92.25) * mm});
            skLineSegment(sketch, "E90.MirrorCS", {"start": v(-15, -92.25) * mm, "end": v(-33, -74.25) * mm});
            skCircle(sketch, "E91.MirrorC", {"center": v(0, -104.25) * mm, "radius": 6 * mm});
            skLineSegment(sketch, "E92.MirrorCS", {"start": v(15, -92.25) * mm, "end": v(33, -74.25) * mm});
            skArc(sketch, "E93.MirrorCS", {"start": v(-15, -104.25) * mm, "mid": v(0, -119.25) * mm, "end": v(15, -104.25) * mm});
            skArc(sketch, "E94.MirrorCS", {"start": v(15, -104.25) * mm, "mid": v(0, -119.25) * mm, "end": v(-15, -104.25) * mm});
            skLineSegment(sketch, "E95.MirrorCS", {"start": v(0, -74.25) * mm, "end": v(0, -104.25) * mm, "construction": true});
            skSolve(sketch);
        }
        {
            var Q0;
            Q0=makeQuery(id+"F16.imprint","IMPRINT",FACE,{"disambiguationData":[TD([[makeQuery(id+"F16.imprint","IMPRINT",EDGE,{"derivedFrom":makeQuery(id+"F1.opExtrude","CAP_EDGE",EDGE,{"disambiguationData":[OSD([sQuery(id+"F0.wireOp",EDGE,"E6")])],"isStart":true})}),-1.0]])]});
            var Q1;
            Q1=makeQuery(id+"F16.imprint","IMPRINT",FACE,{"disambiguationData":[TD([[makeQuery(id+"F16.imprint","IMPRINT",EDGE,{"derivedFrom":makeQuery(id+"F1.opExtrude","CAP_EDGE",EDGE,{"disambiguationData":[OSD([sQuery(id+"F0.wireOp",EDGE,"E4")])],"isStart":true})}),-1.0]])]});
            var Q2;
            Q2=makeQuery(id+"F16.imprint","IMPRINT",FACE,{"disambiguationData":[TD([[makeQuery(id+"F16.imprint","IMPRINT",EDGE,{"derivedFrom":sQuery(id+"F16.wireOp",EDGE,"E84")}),-1.0]])]});
            var Q3;
            Q3=makeQuery(id+"F16.imprint","IMPRINT",FACE,{"disambiguationData":[TD([[makeQuery(id+"F16.imprint","IMPRINT",EDGE,{"derivedFrom":sQuery(id+"F16.wireOp",EDGE,"E88.MirrorCS")}),-1.0]])]});
            extrude(context, id + "F17", {"entities" : qUnion([Q0, Q1, Q2, Q3]), "depth" : 5 * mm});
        }
    });
